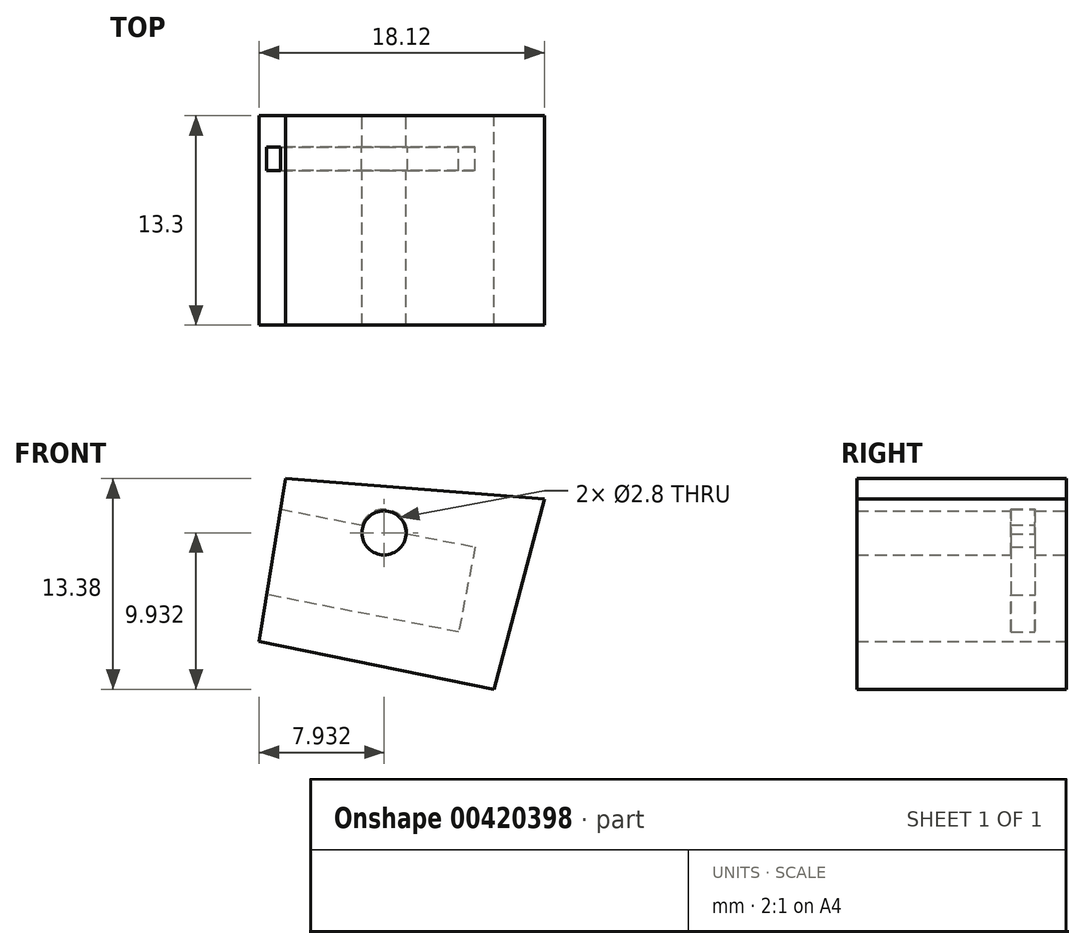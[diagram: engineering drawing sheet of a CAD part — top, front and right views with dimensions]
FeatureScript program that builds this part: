
annotation { "Feature Type Name" : "Feature", "Feature Type Description" : "" }
export const myFeature = defineFeature(function(context is Context, id is Id, definition is map)
    precondition{}
    {
        {
            var Q0;
            Q0=qCreatedBy(makeId("Front.planeOp"),FACE);
            var sketch = newSketch(context, id + "F0", { "sketchPlane" : qUnion([Q0])});
            skArc(sketch, "E0", {"start": v(0.13, 4.4) * mm, "mid": v(0, 4.4) * mm, "end": v(-0.13, 4.4) * mm});
            skLineSegment(sketch, "E1", {"start": v(0.28, 4.51) * mm, "end": v(0.42, 5.1) * mm});
            skLineSegment(sketch, "E2.MirrorCS", {"start": v(-0.28, 4.51) * mm, "end": v(-0.42, 5.1) * mm});
            skPoint(sketch, "E3.visualSharp", {"position": v(0.25, 4.4) * mm});
            skArc(sketch, "E3.filletArc", {"start": v(0.13, 4.4) * mm, "mid": v(0.22, 4.43) * mm, "end": v(0.28, 4.51) * mm});
            skPoint(sketch, "E4.visualSharp", {"position": v(-0.25, 4.4) * mm});
            skArc(sketch, "E4.filletArc", {"start": v(-0.28, 4.51) * mm, "mid": v(-0.22, 4.43) * mm, "end": v(-0.13, 4.4) * mm});
            skPoint(sketch, "E5.visualSharp", {"position": v(0.45, 5.23) * mm});
            skArc(sketch, "E5.filletArc", {"start": v(0.58, 5.22) * mm, "mid": v(0.48, 5.2) * mm, "end": v(0.42, 5.1) * mm});
            skPoint(sketch, "E6.visualSharp", {"position": v(-0.45, 5.23) * mm});
            skArc(sketch, "E6.filletArc", {"start": v(-0.42, 5.1) * mm, "mid": v(-0.48, 5.2) * mm, "end": v(-0.58, 5.22) * mm});
            skArc(sketch, "E7.trimOffspring", {"start": v(1.46, 5.04) * mm, "mid": v(1.02, 5.15) * mm, "end": v(0.58, 5.22) * mm});
            skPoint(sketch, "E8.visualSharp", {"position": v(1.59, 5) * mm});
            skArc(sketch, "E9.1.1", {"start": v(-1.98, 4.06) * mm, "mid": v(-1.9, 4) * mm, "end": v(-1.8, 4.01) * mm});
            skArc(sketch, "E9.1.2", {"start": v(-0.58, 5.22) * mm, "mid": v(-1.02, 5.15) * mm, "end": v(-1.46, 5.04) * mm});
            skArc(sketch, "E9.1.3", {"start": v(-1.56, 4.11) * mm, "mid": v(-1.68, 4.07) * mm, "end": v(-1.8, 4.01) * mm});
            skLineSegment(sketch, "E9.1.4", {"start": v(-1.98, 4.06) * mm, "end": v(-2.34, 4.55) * mm});
            skPoint(sketch, "E9.1.5", {"position": v(-1.91, 3.96) * mm});
            skPoint(sketch, "E9.1.6", {"position": v(-2.42, 4.66) * mm});
            skLineSegment(sketch, "E9.1.7", {"start": v(-1.47, 4.28) * mm, "end": v(-1.57, 4.88) * mm});
            skPoint(sketch, "E9.1.8", {"position": v(-1.59, 5) * mm});
            skArc(sketch, "E9.1.9", {"start": v(-1.56, 4.11) * mm, "mid": v(-1.49, 4.18) * mm, "end": v(-1.47, 4.28) * mm});
            skArc(sketch, "E9.1.10", {"start": v(-1.46, 5.04) * mm, "mid": v(-1.54, 4.98) * mm, "end": v(-1.57, 4.88) * mm});
            skPoint(sketch, "E9.1.11", {"position": v(-1.45, 4.15) * mm});
            skArc(sketch, "E9.1.12", {"start": v(-2.34, 4.55) * mm, "mid": v(-2.43, 4.61) * mm, "end": v(-2.53, 4.6) * mm});
            skPoint(sketch, "E9.2.0", {"position": v(-2.42, 4.66) * mm});
            skArc(sketch, "E9.2.1", {"start": v(-3.39, 3) * mm, "mid": v(-3.3, 2.97) * mm, "end": v(-3.2, 3.02) * mm});
            skArc(sketch, "E9.2.2", {"start": v(-2.53, 4.6) * mm, "mid": v(-2.92, 4.37) * mm, "end": v(-3.28, 4.1) * mm});
            skArc(sketch, "E9.2.3", {"start": v(-3.02, 3.2) * mm, "mid": v(-3.11, 3.11) * mm, "end": v(-3.2, 3.02) * mm});
            skLineSegment(sketch, "E9.2.4", {"start": v(-3.39, 3) * mm, "end": v(-3.9, 3.31) * mm});
            skPoint(sketch, "E9.2.5", {"position": v(-3.28, 2.93) * mm});
            skPoint(sketch, "E9.2.6", {"position": v(-4.02, 3.38) * mm});
            skLineSegment(sketch, "E9.2.7", {"start": v(-3, 3.39) * mm, "end": v(-3.31, 3.9) * mm});
            skPoint(sketch, "E9.2.8", {"position": v(-3.38, 4.02) * mm});
            skArc(sketch, "E9.2.9", {"start": v(-3.02, 3.2) * mm, "mid": v(-2.97, 3.3) * mm, "end": v(-3, 3.39) * mm});
            skArc(sketch, "E9.2.10", {"start": v(-3.28, 4.1) * mm, "mid": v(-3.33, 4) * mm, "end": v(-3.31, 3.9) * mm});
            skPoint(sketch, "E9.2.11", {"position": v(-2.93, 3.28) * mm});
            skArc(sketch, "E9.2.12", {"start": v(-3.9, 3.31) * mm, "mid": v(-4, 3.33) * mm, "end": v(-4.1, 3.28) * mm});
            skPoint(sketch, "E9.3.0", {"position": v(-4.02, 3.38) * mm});
            skArc(sketch, "E9.3.1", {"start": v(-4.28, 1.47) * mm, "mid": v(-4.18, 1.49) * mm, "end": v(-4.11, 1.56) * mm});
            skArc(sketch, "E9.3.2", {"start": v(-4.1, 3.28) * mm, "mid": v(-4.37, 2.92) * mm, "end": v(-4.6, 2.53) * mm});
            skArc(sketch, "E9.3.3", {"start": v(-4.01, 1.8) * mm, "mid": v(-4.07, 1.68) * mm, "end": v(-4.11, 1.56) * mm});
            skLineSegment(sketch, "E9.3.4", {"start": v(-4.28, 1.47) * mm, "end": v(-4.88, 1.57) * mm});
            skPoint(sketch, "E9.3.5", {"position": v(-4.15, 1.45) * mm});
            skPoint(sketch, "E9.3.6", {"position": v(-5, 1.59) * mm});
            skLineSegment(sketch, "E9.3.7", {"start": v(-4.06, 1.98) * mm, "end": v(-4.55, 2.34) * mm});
            skPoint(sketch, "E9.3.8", {"position": v(-4.66, 2.42) * mm});
            skArc(sketch, "E9.3.9", {"start": v(-4.01, 1.8) * mm, "mid": v(-4, 1.9) * mm, "end": v(-4.06, 1.98) * mm});
            skArc(sketch, "E9.3.10", {"start": v(-4.6, 2.53) * mm, "mid": v(-4.61, 2.43) * mm, "end": v(-4.55, 2.34) * mm});
            skPoint(sketch, "E9.3.11", {"position": v(-3.96, 1.91) * mm});
            skArc(sketch, "E9.3.12", {"start": v(-4.88, 1.57) * mm, "mid": v(-4.98, 1.54) * mm, "end": v(-5.04, 1.46) * mm});
            skPoint(sketch, "E9.4.0", {"position": v(-5, 1.59) * mm});
            skArc(sketch, "E9.4.1", {"start": v(-4.51, -0.28) * mm, "mid": v(-4.43, -0.22) * mm, "end": v(-4.4, -0.13) * mm});
            skArc(sketch, "E9.4.2", {"start": v(-5.04, 1.46) * mm, "mid": v(-5.15, 1.02) * mm, "end": v(-5.22, 0.58) * mm});
            skArc(sketch, "E9.4.3", {"start": v(-4.4, 0.13) * mm, "mid": v(-4.4, 0) * mm, "end": v(-4.4, -0.13) * mm});
            skLineSegment(sketch, "E9.4.4", {"start": v(-4.51, -0.28) * mm, "end": v(-5.1, -0.42) * mm});
            skPoint(sketch, "E9.4.5", {"position": v(-4.4, -0.25) * mm});
            skPoint(sketch, "E9.4.6", {"position": v(-5.23, -0.45) * mm});
            skLineSegment(sketch, "E9.4.7", {"start": v(-4.51, 0.28) * mm, "end": v(-5.1, 0.42) * mm});
            skPoint(sketch, "E9.4.8", {"position": v(-5.23, 0.45) * mm});
            skArc(sketch, "E9.4.9", {"start": v(-4.4, 0.13) * mm, "mid": v(-4.43, 0.22) * mm, "end": v(-4.51, 0.28) * mm});
            skArc(sketch, "E9.4.10", {"start": v(-5.22, 0.58) * mm, "mid": v(-5.2, 0.48) * mm, "end": v(-5.1, 0.42) * mm});
            skPoint(sketch, "E9.4.11", {"position": v(-4.4, 0.25) * mm});
            skArc(sketch, "E9.4.12", {"start": v(-5.1, -0.42) * mm, "mid": v(-5.2, -0.48) * mm, "end": v(-5.22, -0.58) * mm});
            skPoint(sketch, "E9.5.0", {"position": v(-5.23, -0.45) * mm});
            skArc(sketch, "E9.5.1", {"start": v(-4.06, -1.98) * mm, "mid": v(-4, -1.9) * mm, "end": v(-4.01, -1.8) * mm});
            skArc(sketch, "E9.5.2", {"start": v(-5.22, -0.58) * mm, "mid": v(-5.15, -1.02) * mm, "end": v(-5.04, -1.46) * mm});
            skArc(sketch, "E9.5.3", {"start": v(-4.11, -1.56) * mm, "mid": v(-4.07, -1.68) * mm, "end": v(-4.01, -1.8) * mm});
            skLineSegment(sketch, "E9.5.4", {"start": v(-4.06, -1.98) * mm, "end": v(-4.55, -2.34) * mm});
            skPoint(sketch, "E9.5.5", {"position": v(-3.96, -1.91) * mm});
            skPoint(sketch, "E9.5.6", {"position": v(-4.66, -2.42) * mm});
            skLineSegment(sketch, "E9.5.7", {"start": v(-4.28, -1.47) * mm, "end": v(-4.88, -1.57) * mm});
            skPoint(sketch, "E9.5.8", {"position": v(-5, -1.59) * mm});
            skArc(sketch, "E9.5.9", {"start": v(-4.11, -1.56) * mm, "mid": v(-4.18, -1.49) * mm, "end": v(-4.28, -1.47) * mm});
            skArc(sketch, "E9.5.10", {"start": v(-5.04, -1.46) * mm, "mid": v(-4.98, -1.54) * mm, "end": v(-4.88, -1.57) * mm});
            skPoint(sketch, "E9.5.11", {"position": v(-4.15, -1.45) * mm});
            skArc(sketch, "E9.5.12", {"start": v(-4.55, -2.34) * mm, "mid": v(-4.61, -2.43) * mm, "end": v(-4.6, -2.53) * mm});
            skPoint(sketch, "E9.6.0", {"position": v(-4.66, -2.42) * mm});
            skArc(sketch, "E9.6.1", {"start": v(-3, -3.39) * mm, "mid": v(-2.97, -3.3) * mm, "end": v(-3.02, -3.2) * mm});
            skArc(sketch, "E9.6.2", {"start": v(-4.6, -2.53) * mm, "mid": v(-4.37, -2.92) * mm, "end": v(-4.1, -3.28) * mm});
            skArc(sketch, "E9.6.3", {"start": v(-3.2, -3.02) * mm, "mid": v(-3.11, -3.11) * mm, "end": v(-3.02, -3.2) * mm});
            skLineSegment(sketch, "E9.6.4", {"start": v(-3, -3.39) * mm, "end": v(-3.31, -3.9) * mm});
            skPoint(sketch, "E9.6.5", {"position": v(-2.93, -3.28) * mm});
            skPoint(sketch, "E9.6.6", {"position": v(-3.38, -4.02) * mm});
            skLineSegment(sketch, "E9.6.7", {"start": v(-3.39, -3) * mm, "end": v(-3.9, -3.31) * mm});
            skPoint(sketch, "E9.6.8", {"position": v(-4.02, -3.38) * mm});
            skArc(sketch, "E9.6.9", {"start": v(-3.2, -3.02) * mm, "mid": v(-3.3, -2.97) * mm, "end": v(-3.39, -3) * mm});
            skArc(sketch, "E9.6.10", {"start": v(-4.1, -3.28) * mm, "mid": v(-4, -3.33) * mm, "end": v(-3.9, -3.31) * mm});
            skPoint(sketch, "E9.6.11", {"position": v(-3.28, -2.93) * mm});
            skArc(sketch, "E9.6.12", {"start": v(-3.31, -3.9) * mm, "mid": v(-3.33, -4) * mm, "end": v(-3.28, -4.1) * mm});
            skPoint(sketch, "E9.7.0", {"position": v(-3.38, -4.02) * mm});
            skArc(sketch, "E9.7.1", {"start": v(-1.47, -4.28) * mm, "mid": v(-1.49, -4.18) * mm, "end": v(-1.56, -4.11) * mm});
            skArc(sketch, "E9.7.2", {"start": v(-3.28, -4.1) * mm, "mid": v(-2.92, -4.37) * mm, "end": v(-2.53, -4.6) * mm});
            skArc(sketch, "E9.7.3", {"start": v(-1.8, -4.01) * mm, "mid": v(-1.68, -4.07) * mm, "end": v(-1.56, -4.11) * mm});
            skLineSegment(sketch, "E9.7.4", {"start": v(-1.47, -4.28) * mm, "end": v(-1.57, -4.88) * mm});
            skPoint(sketch, "E9.7.5", {"position": v(-1.45, -4.15) * mm});
            skPoint(sketch, "E9.7.6", {"position": v(-1.59, -5) * mm});
            skLineSegment(sketch, "E9.7.7", {"start": v(-1.98, -4.06) * mm, "end": v(-2.34, -4.55) * mm});
            skPoint(sketch, "E9.7.8", {"position": v(-2.42, -4.66) * mm});
            skArc(sketch, "E9.7.9", {"start": v(-1.8, -4.01) * mm, "mid": v(-1.9, -4) * mm, "end": v(-1.98, -4.06) * mm});
            skArc(sketch, "E9.7.10", {"start": v(-2.53, -4.6) * mm, "mid": v(-2.43, -4.61) * mm, "end": v(-2.34, -4.55) * mm});
            skPoint(sketch, "E9.7.11", {"position": v(-1.91, -3.96) * mm});
            skArc(sketch, "E9.7.12", {"start": v(-1.57, -4.88) * mm, "mid": v(-1.54, -4.98) * mm, "end": v(-1.46, -5.04) * mm});
            skPoint(sketch, "E9.8.0", {"position": v(-1.59, -5) * mm});
            skArc(sketch, "E9.8.1", {"start": v(0.28, -4.51) * mm, "mid": v(0.22, -4.43) * mm, "end": v(0.13, -4.4) * mm});
            skArc(sketch, "E9.8.2", {"start": v(-1.46, -5.04) * mm, "mid": v(-1.02, -5.15) * mm, "end": v(-0.58, -5.22) * mm});
            skArc(sketch, "E9.8.3", {"start": v(-0.13, -4.4) * mm, "mid": v(0, -4.4) * mm, "end": v(0.13, -4.4) * mm});
            skLineSegment(sketch, "E9.8.4", {"start": v(0.28, -4.51) * mm, "end": v(0.42, -5.1) * mm});
            skPoint(sketch, "E9.8.5", {"position": v(0.25, -4.4) * mm});
            skPoint(sketch, "E9.8.6", {"position": v(0.45, -5.23) * mm});
            skLineSegment(sketch, "E9.8.7", {"start": v(-0.28, -4.51) * mm, "end": v(-0.42, -5.1) * mm});
            skPoint(sketch, "E9.8.8", {"position": v(-0.45, -5.23) * mm});
            skArc(sketch, "E9.8.9", {"start": v(-0.13, -4.4) * mm, "mid": v(-0.22, -4.43) * mm, "end": v(-0.28, -4.51) * mm});
            skArc(sketch, "E9.8.10", {"start": v(-0.58, -5.22) * mm, "mid": v(-0.48, -5.2) * mm, "end": v(-0.42, -5.1) * mm});
            skPoint(sketch, "E9.8.11", {"position": v(-0.25, -4.4) * mm});
            skArc(sketch, "E9.8.12", {"start": v(0.42, -5.1) * mm, "mid": v(0.48, -5.2) * mm, "end": v(0.58, -5.22) * mm});
            skPoint(sketch, "E9.9.0", {"position": v(0.45, -5.23) * mm});
            skArc(sketch, "E9.9.1", {"start": v(1.98, -4.06) * mm, "mid": v(1.9, -4) * mm, "end": v(1.8, -4.01) * mm});
            skArc(sketch, "E9.9.2", {"start": v(0.58, -5.22) * mm, "mid": v(1.02, -5.15) * mm, "end": v(1.46, -5.04) * mm});
            skArc(sketch, "E9.9.3", {"start": v(1.56, -4.11) * mm, "mid": v(1.68, -4.07) * mm, "end": v(1.8, -4.01) * mm});
            skLineSegment(sketch, "E9.9.4", {"start": v(1.98, -4.06) * mm, "end": v(2.34, -4.55) * mm});
            skPoint(sketch, "E9.9.5", {"position": v(1.91, -3.96) * mm});
            skPoint(sketch, "E9.9.6", {"position": v(2.42, -4.66) * mm});
            skLineSegment(sketch, "E9.9.7", {"start": v(1.47, -4.28) * mm, "end": v(1.57, -4.88) * mm});
            skPoint(sketch, "E9.9.8", {"position": v(1.59, -5) * mm});
            skArc(sketch, "E9.9.9", {"start": v(1.56, -4.11) * mm, "mid": v(1.49, -4.18) * mm, "end": v(1.47, -4.28) * mm});
            skArc(sketch, "E9.9.10", {"start": v(1.46, -5.04) * mm, "mid": v(1.54, -4.98) * mm, "end": v(1.57, -4.88) * mm});
            skPoint(sketch, "E9.9.11", {"position": v(1.45, -4.15) * mm});
            skArc(sketch, "E9.9.12", {"start": v(2.34, -4.55) * mm, "mid": v(2.43, -4.61) * mm, "end": v(2.53, -4.6) * mm});
            skPoint(sketch, "E9.10.0", {"position": v(2.42, -4.66) * mm});
            skArc(sketch, "E9.10.1", {"start": v(3.39, -3) * mm, "mid": v(3.3, -2.97) * mm, "end": v(3.2, -3.02) * mm});
            skArc(sketch, "E9.10.2", {"start": v(2.53, -4.6) * mm, "mid": v(2.92, -4.37) * mm, "end": v(3.28, -4.1) * mm});
            skArc(sketch, "E9.10.3", {"start": v(3.02, -3.2) * mm, "mid": v(3.11, -3.11) * mm, "end": v(3.2, -3.02) * mm});
            skLineSegment(sketch, "E9.10.4", {"start": v(3.39, -3) * mm, "end": v(3.9, -3.31) * mm});
            skPoint(sketch, "E9.10.5", {"position": v(3.28, -2.93) * mm});
            skPoint(sketch, "E9.10.6", {"position": v(4.02, -3.38) * mm});
            skLineSegment(sketch, "E9.10.7", {"start": v(3, -3.39) * mm, "end": v(3.31, -3.9) * mm});
            skPoint(sketch, "E9.10.8", {"position": v(3.38, -4.02) * mm});
            skArc(sketch, "E9.10.9", {"start": v(3.02, -3.2) * mm, "mid": v(2.97, -3.3) * mm, "end": v(3, -3.39) * mm});
            skArc(sketch, "E9.10.10", {"start": v(3.28, -4.1) * mm, "mid": v(3.33, -4) * mm, "end": v(3.31, -3.9) * mm});
            skPoint(sketch, "E9.10.11", {"position": v(2.93, -3.28) * mm});
            skArc(sketch, "E9.10.12", {"start": v(3.9, -3.31) * mm, "mid": v(4, -3.33) * mm, "end": v(4.1, -3.28) * mm});
            skPoint(sketch, "E9.11.0", {"position": v(4.02, -3.38) * mm});
            skArc(sketch, "E9.11.1", {"start": v(4.28, -1.47) * mm, "mid": v(4.18, -1.49) * mm, "end": v(4.11, -1.56) * mm});
            skArc(sketch, "E9.11.2", {"start": v(4.1, -3.28) * mm, "mid": v(4.37, -2.92) * mm, "end": v(4.6, -2.53) * mm});
            skArc(sketch, "E9.11.3", {"start": v(4.01, -1.8) * mm, "mid": v(4.07, -1.68) * mm, "end": v(4.11, -1.56) * mm});
            skLineSegment(sketch, "E9.11.4", {"start": v(4.28, -1.47) * mm, "end": v(4.88, -1.57) * mm});
            skPoint(sketch, "E9.11.5", {"position": v(4.15, -1.45) * mm});
            skPoint(sketch, "E9.11.6", {"position": v(5, -1.59) * mm});
            skLineSegment(sketch, "E9.11.7", {"start": v(4.06, -1.98) * mm, "end": v(4.55, -2.34) * mm});
            skPoint(sketch, "E9.11.8", {"position": v(4.66, -2.42) * mm});
            skArc(sketch, "E9.11.9", {"start": v(4.01, -1.8) * mm, "mid": v(4, -1.9) * mm, "end": v(4.06, -1.98) * mm});
            skArc(sketch, "E9.11.10", {"start": v(4.6, -2.53) * mm, "mid": v(4.61, -2.43) * mm, "end": v(4.55, -2.34) * mm});
            skPoint(sketch, "E9.11.11", {"position": v(3.96, -1.91) * mm});
            skArc(sketch, "E9.11.12", {"start": v(4.88, -1.57) * mm, "mid": v(4.98, -1.54) * mm, "end": v(5.04, -1.46) * mm});
            skPoint(sketch, "E9.12.0", {"position": v(5, -1.59) * mm});
            skArc(sketch, "E9.12.1", {"start": v(4.51, 0.28) * mm, "mid": v(4.43, 0.22) * mm, "end": v(4.4, 0.13) * mm});
            skArc(sketch, "E9.12.2", {"start": v(5.04, -1.46) * mm, "mid": v(5.15, -1.02) * mm, "end": v(5.22, -0.58) * mm});
            skArc(sketch, "E9.12.3", {"start": v(4.4, -0.13) * mm, "mid": v(4.4, 0) * mm, "end": v(4.4, 0.13) * mm});
            skLineSegment(sketch, "E9.12.4", {"start": v(4.51, 0.28) * mm, "end": v(5.1, 0.42) * mm});
            skPoint(sketch, "E9.12.5", {"position": v(4.4, 0.25) * mm});
            skPoint(sketch, "E9.12.6", {"position": v(5.23, 0.45) * mm});
            skLineSegment(sketch, "E9.12.7", {"start": v(4.51, -0.28) * mm, "end": v(5.1, -0.42) * mm});
            skPoint(sketch, "E9.12.8", {"position": v(5.23, -0.45) * mm});
            skArc(sketch, "E9.12.9", {"start": v(4.4, -0.13) * mm, "mid": v(4.43, -0.22) * mm, "end": v(4.51, -0.28) * mm});
            skArc(sketch, "E9.12.10", {"start": v(5.22, -0.58) * mm, "mid": v(5.2, -0.48) * mm, "end": v(5.1, -0.42) * mm});
            skPoint(sketch, "E9.12.11", {"position": v(4.4, -0.25) * mm});
            skArc(sketch, "E9.12.12", {"start": v(5.1, 0.42) * mm, "mid": v(5.2, 0.48) * mm, "end": v(5.22, 0.58) * mm});
            skPoint(sketch, "E9.13.0", {"position": v(5.23, 0.45) * mm});
            skArc(sketch, "E9.13.1", {"start": v(4.06, 1.98) * mm, "mid": v(4, 1.9) * mm, "end": v(4.01, 1.8) * mm});
            skArc(sketch, "E9.13.2", {"start": v(5.22, 0.58) * mm, "mid": v(5.15, 1.02) * mm, "end": v(5.04, 1.46) * mm});
            skArc(sketch, "E9.13.3", {"start": v(4.11, 1.56) * mm, "mid": v(4.07, 1.68) * mm, "end": v(4.01, 1.8) * mm});
            skLineSegment(sketch, "E9.13.4", {"start": v(4.06, 1.98) * mm, "end": v(4.55, 2.34) * mm});
            skPoint(sketch, "E9.13.5", {"position": v(3.96, 1.91) * mm});
            skPoint(sketch, "E9.13.6", {"position": v(4.66, 2.42) * mm});
            skLineSegment(sketch, "E9.13.7", {"start": v(4.28, 1.47) * mm, "end": v(4.88, 1.57) * mm});
            skPoint(sketch, "E9.13.8", {"position": v(5, 1.59) * mm});
            skArc(sketch, "E9.13.9", {"start": v(4.11, 1.56) * mm, "mid": v(4.18, 1.49) * mm, "end": v(4.28, 1.47) * mm});
            skArc(sketch, "E9.13.10", {"start": v(5.04, 1.46) * mm, "mid": v(4.98, 1.54) * mm, "end": v(4.88, 1.57) * mm});
            skPoint(sketch, "E9.13.11", {"position": v(4.15, 1.45) * mm});
            skArc(sketch, "E9.13.12", {"start": v(4.55, 2.34) * mm, "mid": v(4.61, 2.43) * mm, "end": v(4.6, 2.53) * mm});
            skPoint(sketch, "E9.14.0", {"position": v(4.66, 2.42) * mm});
            skArc(sketch, "E9.14.1", {"start": v(3, 3.39) * mm, "mid": v(2.97, 3.3) * mm, "end": v(3.02, 3.2) * mm});
            skArc(sketch, "E9.14.2", {"start": v(4.6, 2.53) * mm, "mid": v(4.37, 2.92) * mm, "end": v(4.1, 3.28) * mm});
            skArc(sketch, "E9.14.3", {"start": v(3.2, 3.02) * mm, "mid": v(3.11, 3.11) * mm, "end": v(3.02, 3.2) * mm});
            skLineSegment(sketch, "E9.14.4", {"start": v(3, 3.39) * mm, "end": v(3.31, 3.9) * mm});
            skPoint(sketch, "E9.14.5", {"position": v(2.93, 3.28) * mm});
            skPoint(sketch, "E9.14.6", {"position": v(3.38, 4.02) * mm});
            skLineSegment(sketch, "E9.14.7", {"start": v(3.39, 3) * mm, "end": v(3.9, 3.31) * mm});
            skPoint(sketch, "E9.14.8", {"position": v(4.02, 3.38) * mm});
            skArc(sketch, "E9.14.9", {"start": v(3.2, 3.02) * mm, "mid": v(3.3, 2.97) * mm, "end": v(3.39, 3) * mm});
            skArc(sketch, "E9.14.10", {"start": v(4.1, 3.28) * mm, "mid": v(4, 3.33) * mm, "end": v(3.9, 3.31) * mm});
            skPoint(sketch, "E9.14.11", {"position": v(3.28, 2.93) * mm});
            skArc(sketch, "E9.14.12", {"start": v(3.31, 3.9) * mm, "mid": v(3.33, 4) * mm, "end": v(3.28, 4.1) * mm});
            skPoint(sketch, "E9.15.0", {"position": v(3.38, 4.02) * mm});
            skArc(sketch, "E9.15.1", {"start": v(1.47, 4.28) * mm, "mid": v(1.49, 4.18) * mm, "end": v(1.56, 4.11) * mm});
            skArc(sketch, "E9.15.2", {"start": v(3.28, 4.1) * mm, "mid": v(2.92, 4.37) * mm, "end": v(2.53, 4.6) * mm});
            skArc(sketch, "E9.15.3", {"start": v(1.8, 4.01) * mm, "mid": v(1.68, 4.07) * mm, "end": v(1.56, 4.11) * mm});
            skLineSegment(sketch, "E9.15.4", {"start": v(1.47, 4.28) * mm, "end": v(1.57, 4.88) * mm});
            skPoint(sketch, "E9.15.5", {"position": v(1.45, 4.15) * mm});
            skLineSegment(sketch, "E9.15.7", {"start": v(1.98, 4.06) * mm, "end": v(2.34, 4.55) * mm});
            skPoint(sketch, "E9.15.8", {"position": v(2.42, 4.66) * mm});
            skArc(sketch, "E9.15.9", {"start": v(1.8, 4.01) * mm, "mid": v(1.9, 4) * mm, "end": v(1.98, 4.06) * mm});
            skArc(sketch, "E9.15.10", {"start": v(2.53, 4.6) * mm, "mid": v(2.43, 4.61) * mm, "end": v(2.34, 4.55) * mm});
            skPoint(sketch, "E9.15.11", {"position": v(1.91, 3.96) * mm});
            skArc(sketch, "E9.15.12", {"start": v(1.57, 4.88) * mm, "mid": v(1.54, 4.98) * mm, "end": v(1.46, 5.04) * mm});
            skCircle(sketch, "E10", {"center": v(0, 0) * mm, "radius": 7.5 * mm});
            skSolve(sketch);
        }
        {
            var Q0;
            Q0=qSketchRegion(id+"F0",true);
            extrude(context, id + "F1", {"entities" : qUnion([Q0]), "depth" : 10 * mm});
        }
        {
            var Q0;
            Q0=makeQuery(id+"F1.opExtrude","CAP_FACE",FACE,{"disambiguationData":[OSD([sQuery(id+"F0.wireOp",EDGE,"E0"),sQuery(id+"F0.wireOp",EDGE,"E1"),sQuery(id+"F0.wireOp",EDGE,"E2.MirrorCS"),sQuery(id+"F0.wireOp",EDGE,"E3.filletArc"),sQuery(id+"F0.wireOp",EDGE,"E4.filletArc"),sQuery(id+"F0.wireOp",EDGE,"E5.filletArc"),sQuery(id+"F0.wireOp",EDGE,"E6.filletArc"),sQuery(id+"F0.wireOp",EDGE,"E7.trimOffspring"),sQuery(id+"F0.wireOp",EDGE,"E9.1.1"),sQuery(id+"F0.wireOp",EDGE,"E9.1.2"),sQuery(id+"F0.wireOp",EDGE,"E9.1.3"),sQuery(id+"F0.wireOp",EDGE,"E9.1.4"),sQuery(id+"F0.wireOp",EDGE,"E9.1.7"),sQuery(id+"F0.wireOp",EDGE,"E9.1.9"),sQuery(id+"F0.wireOp",EDGE,"E9.1.10"),sQuery(id+"F0.wireOp",EDGE,"E9.1.12"),sQuery(id+"F0.wireOp",EDGE,"E9.2.1"),sQuery(id+"F0.wireOp",EDGE,"E9.2.2"),sQuery(id+"F0.wireOp",EDGE,"E9.2.3"),sQuery(id+"F0.wireOp",EDGE,"E9.2.4"),sQuery(id+"F0.wireOp",EDGE,"E9.2.7"),sQuery(id+"F0.wireOp",EDGE,"E9.2.9"),sQuery(id+"F0.wireOp",EDGE,"E9.2.10"),sQuery(id+"F0.wireOp",EDGE,"E9.2.12"),sQuery(id+"F0.wireOp",EDGE,"E9.3.1"),sQuery(id+"F0.wireOp",EDGE,"E9.3.2"),sQuery(id+"F0.wireOp",EDGE,"E9.3.3"),sQuery(id+"F0.wireOp",EDGE,"E9.3.4"),sQuery(id+"F0.wireOp",EDGE,"E9.3.7"),sQuery(id+"F0.wireOp",EDGE,"E9.3.9"),sQuery(id+"F0.wireOp",EDGE,"E9.3.10"),sQuery(id+"F0.wireOp",EDGE,"E9.3.12"),sQuery(id+"F0.wireOp",EDGE,"E9.4.1"),sQuery(id+"F0.wireOp",EDGE,"E9.4.2"),sQuery(id+"F0.wireOp",EDGE,"E9.4.3"),sQuery(id+"F0.wireOp",EDGE,"E9.4.4"),sQuery(id+"F0.wireOp",EDGE,"E9.4.7"),sQuery(id+"F0.wireOp",EDGE,"E9.4.9"),sQuery(id+"F0.wireOp",EDGE,"E9.4.10"),sQuery(id+"F0.wireOp",EDGE,"E9.4.12"),sQuery(id+"F0.wireOp",EDGE,"E9.5.1"),sQuery(id+"F0.wireOp",EDGE,"E9.5.2"),sQuery(id+"F0.wireOp",EDGE,"E9.5.3"),sQuery(id+"F0.wireOp",EDGE,"E9.5.4"),sQuery(id+"F0.wireOp",EDGE,"E9.5.7"),sQuery(id+"F0.wireOp",EDGE,"E9.5.9"),sQuery(id+"F0.wireOp",EDGE,"E9.5.10"),sQuery(id+"F0.wireOp",EDGE,"E9.5.12"),sQuery(id+"F0.wireOp",EDGE,"E9.6.1"),sQuery(id+"F0.wireOp",EDGE,"E9.6.2"),sQuery(id+"F0.wireOp",EDGE,"E9.6.3"),sQuery(id+"F0.wireOp",EDGE,"E9.6.4"),sQuery(id+"F0.wireOp",EDGE,"E9.6.7"),sQuery(id+"F0.wireOp",EDGE,"E9.6.9"),sQuery(id+"F0.wireOp",EDGE,"E9.6.10"),sQuery(id+"F0.wireOp",EDGE,"E9.6.12"),sQuery(id+"F0.wireOp",EDGE,"E9.7.1"),sQuery(id+"F0.wireOp",EDGE,"E9.7.2"),sQuery(id+"F0.wireOp",EDGE,"E9.7.3"),sQuery(id+"F0.wireOp",EDGE,"E9.7.4"),sQuery(id+"F0.wireOp",EDGE,"E9.7.7"),sQuery(id+"F0.wireOp",EDGE,"E9.7.9"),sQuery(id+"F0.wireOp",EDGE,"E9.7.10"),sQuery(id+"F0.wireOp",EDGE,"E9.7.12"),sQuery(id+"F0.wireOp",EDGE,"E9.8.1"),sQuery(id+"F0.wireOp",EDGE,"E9.8.2"),sQuery(id+"F0.wireOp",EDGE,"E9.8.3"),sQuery(id+"F0.wireOp",EDGE,"E9.8.4"),sQuery(id+"F0.wireOp",EDGE,"E9.8.7"),sQuery(id+"F0.wireOp",EDGE,"E9.8.9"),sQuery(id+"F0.wireOp",EDGE,"E9.8.10"),sQuery(id+"F0.wireOp",EDGE,"E9.8.12"),sQuery(id+"F0.wireOp",EDGE,"E9.9.1"),sQuery(id+"F0.wireOp",EDGE,"E9.9.2"),sQuery(id+"F0.wireOp",EDGE,"E9.9.3"),sQuery(id+"F0.wireOp",EDGE,"E9.9.4"),sQuery(id+"F0.wireOp",EDGE,"E9.9.7"),sQuery(id+"F0.wireOp",EDGE,"E9.9.9"),sQuery(id+"F0.wireOp",EDGE,"E9.9.10"),sQuery(id+"F0.wireOp",EDGE,"E9.9.12"),sQuery(id+"F0.wireOp",EDGE,"E9.10.1"),sQuery(id+"F0.wireOp",EDGE,"E9.10.2"),sQuery(id+"F0.wireOp",EDGE,"E9.10.3"),sQuery(id+"F0.wireOp",EDGE,"E9.10.4"),sQuery(id+"F0.wireOp",EDGE,"E9.10.7"),sQuery(id+"F0.wireOp",EDGE,"E9.10.9"),sQuery(id+"F0.wireOp",EDGE,"E9.10.10"),sQuery(id+"F0.wireOp",EDGE,"E9.10.12"),sQuery(id+"F0.wireOp",EDGE,"E9.11.1"),sQuery(id+"F0.wireOp",EDGE,"E9.11.2"),sQuery(id+"F0.wireOp",EDGE,"E9.11.3"),sQuery(id+"F0.wireOp",EDGE,"E9.11.4"),sQuery(id+"F0.wireOp",EDGE,"E9.11.7"),sQuery(id+"F0.wireOp",EDGE,"E9.11.9"),sQuery(id+"F0.wireOp",EDGE,"E9.11.10"),sQuery(id+"F0.wireOp",EDGE,"E9.11.12"),sQuery(id+"F0.wireOp",EDGE,"E9.12.1"),sQuery(id+"F0.wireOp",EDGE,"E9.12.2"),sQuery(id+"F0.wireOp",EDGE,"E9.12.3"),sQuery(id+"F0.wireOp",EDGE,"E9.12.4"),sQuery(id+"F0.wireOp",EDGE,"E9.12.7"),sQuery(id+"F0.wireOp",EDGE,"E9.12.9"),sQuery(id+"F0.wireOp",EDGE,"E9.12.10"),sQuery(id+"F0.wireOp",EDGE,"E9.12.12"),sQuery(id+"F0.wireOp",EDGE,"E9.13.1"),sQuery(id+"F0.wireOp",EDGE,"E9.13.2"),sQuery(id+"F0.wireOp",EDGE,"E9.13.3"),sQuery(id+"F0.wireOp",EDGE,"E9.13.4"),sQuery(id+"F0.wireOp",EDGE,"E9.13.7"),sQuery(id+"F0.wireOp",EDGE,"E9.13.9"),sQuery(id+"F0.wireOp",EDGE,"E9.13.10"),sQuery(id+"F0.wireOp",EDGE,"E9.13.12"),sQuery(id+"F0.wireOp",EDGE,"E9.14.1"),sQuery(id+"F0.wireOp",EDGE,"E9.14.2"),sQuery(id+"F0.wireOp",EDGE,"E9.14.3"),sQuery(id+"F0.wireOp",EDGE,"E9.14.4"),sQuery(id+"F0.wireOp",EDGE,"E9.14.7"),sQuery(id+"F0.wireOp",EDGE,"E9.14.9"),sQuery(id+"F0.wireOp",EDGE,"E9.14.10"),sQuery(id+"F0.wireOp",EDGE,"E9.14.12"),sQuery(id+"F0.wireOp",EDGE,"E9.15.1"),sQuery(id+"F0.wireOp",EDGE,"E9.15.2"),sQuery(id+"F0.wireOp",EDGE,"E9.15.3"),sQuery(id+"F0.wireOp",EDGE,"E9.15.4"),sQuery(id+"F0.wireOp",EDGE,"E9.15.7"),sQuery(id+"F0.wireOp",EDGE,"E9.15.9"),sQuery(id+"F0.wireOp",EDGE,"E9.15.10"),sQuery(id+"F0.wireOp",EDGE,"E9.15.12"),sQuery(id+"F0.wireOp",EDGE,"E10")])],"isStart":false});
            var sketch = newSketch(context, id + "F2", { "sketchPlane" : qUnion([Q0])});
            skArc(sketch, "E11", {"start": v(72.38, -28.85) * mm, "mid": v(71.17, -27.32) * mm, "end": v(69.47, -28.29) * mm});
            skPoint(sketch, "E12.orphan", {"position": v(59.69, -35.02) * mm});
            skPoint(sketch, "E13.orphan", {"position": v(63.63, -25.26) * mm});
            skLineSegment(sketch, "E14", {"start": v(64.62, -25.34) * mm, "end": v(81.07, -26.63) * mm});
            skLineSegment(sketch, "E15", {"start": v(62.95, -35.68) * mm, "end": v(77.88, -38.72) * mm});
            skLineSegment(sketch, "E16", {"start": v(64.62, -25.34) * mm, "end": v(64.3, -27.28) * mm});
            skLineSegment(sketch, "E17", {"start": v(64.3, -27.28) * mm, "end": v(69.47, -28.29) * mm});
            skLineSegment(sketch, "E18", {"start": v(76.67, -29.68) * mm, "end": v(75.62, -35.08) * mm});
            skLineSegment(sketch, "E19", {"start": v(75.62, -35.08) * mm, "end": v(63.43, -32.72) * mm});
            skLineSegment(sketch, "E20.trimOffspring", {"start": v(63.43, -32.72) * mm, "end": v(62.95, -35.68) * mm});
            skLineSegment(sketch, "E21.trimOffspring", {"start": v(72.38, -28.85) * mm, "end": v(76.67, -29.68) * mm});
            skLineSegment(sketch, "E22", {"start": v(81.07, -26.63) * mm, "end": v(77.88, -38.72) * mm});
            skPoint(sketch, "E23.center.orphan", {"position": v(46.18, -23.89) * mm});
            skSolve(sketch);
        }
        {
            var Q0;
            Q0=makeQuery(id+"F1.opExtrude","SWEPT_BODY",BODY,{"disambiguationData":[OSD([sQuery(id+"F0.wireOp",EDGE,"E0"),sQuery(id+"F0.wireOp",EDGE,"E1"),sQuery(id+"F0.wireOp",EDGE,"E2.MirrorCS"),sQuery(id+"F0.wireOp",EDGE,"E3.filletArc"),sQuery(id+"F0.wireOp",EDGE,"E4.filletArc"),sQuery(id+"F0.wireOp",EDGE,"E5.filletArc"),sQuery(id+"F0.wireOp",EDGE,"E6.filletArc"),sQuery(id+"F0.wireOp",EDGE,"E7.trimOffspring"),sQuery(id+"F0.wireOp",EDGE,"E9.1.1"),sQuery(id+"F0.wireOp",EDGE,"E9.1.2"),sQuery(id+"F0.wireOp",EDGE,"E9.1.3"),sQuery(id+"F0.wireOp",EDGE,"E9.1.4"),sQuery(id+"F0.wireOp",EDGE,"E9.1.7"),sQuery(id+"F0.wireOp",EDGE,"E9.1.9"),sQuery(id+"F0.wireOp",EDGE,"E9.1.10"),sQuery(id+"F0.wireOp",EDGE,"E9.1.12"),sQuery(id+"F0.wireOp",EDGE,"E9.2.1"),sQuery(id+"F0.wireOp",EDGE,"E9.2.2"),sQuery(id+"F0.wireOp",EDGE,"E9.2.3"),sQuery(id+"F0.wireOp",EDGE,"E9.2.4"),sQuery(id+"F0.wireOp",EDGE,"E9.2.7"),sQuery(id+"F0.wireOp",EDGE,"E9.2.9"),sQuery(id+"F0.wireOp",EDGE,"E9.2.10"),sQuery(id+"F0.wireOp",EDGE,"E9.2.12"),sQuery(id+"F0.wireOp",EDGE,"E9.3.1"),sQuery(id+"F0.wireOp",EDGE,"E9.3.2"),sQuery(id+"F0.wireOp",EDGE,"E9.3.3"),sQuery(id+"F0.wireOp",EDGE,"E9.3.4"),sQuery(id+"F0.wireOp",EDGE,"E9.3.7"),sQuery(id+"F0.wireOp",EDGE,"E9.3.9"),sQuery(id+"F0.wireOp",EDGE,"E9.3.10"),sQuery(id+"F0.wireOp",EDGE,"E9.3.12"),sQuery(id+"F0.wireOp",EDGE,"E9.4.1"),sQuery(id+"F0.wireOp",EDGE,"E9.4.2"),sQuery(id+"F0.wireOp",EDGE,"E9.4.3"),sQuery(id+"F0.wireOp",EDGE,"E9.4.4"),sQuery(id+"F0.wireOp",EDGE,"E9.4.7"),sQuery(id+"F0.wireOp",EDGE,"E9.4.9"),sQuery(id+"F0.wireOp",EDGE,"E9.4.10"),sQuery(id+"F0.wireOp",EDGE,"E9.4.12"),sQuery(id+"F0.wireOp",EDGE,"E9.5.1"),sQuery(id+"F0.wireOp",EDGE,"E9.5.2"),sQuery(id+"F0.wireOp",EDGE,"E9.5.3"),sQuery(id+"F0.wireOp",EDGE,"E9.5.4"),sQuery(id+"F0.wireOp",EDGE,"E9.5.7"),sQuery(id+"F0.wireOp",EDGE,"E9.5.9"),sQuery(id+"F0.wireOp",EDGE,"E9.5.10"),sQuery(id+"F0.wireOp",EDGE,"E9.5.12"),sQuery(id+"F0.wireOp",EDGE,"E9.6.1"),sQuery(id+"F0.wireOp",EDGE,"E9.6.2"),sQuery(id+"F0.wireOp",EDGE,"E9.6.3"),sQuery(id+"F0.wireOp",EDGE,"E9.6.4"),sQuery(id+"F0.wireOp",EDGE,"E9.6.7"),sQuery(id+"F0.wireOp",EDGE,"E9.6.9"),sQuery(id+"F0.wireOp",EDGE,"E9.6.10"),sQuery(id+"F0.wireOp",EDGE,"E9.6.12"),sQuery(id+"F0.wireOp",EDGE,"E9.7.1"),sQuery(id+"F0.wireOp",EDGE,"E9.7.2"),sQuery(id+"F0.wireOp",EDGE,"E9.7.3"),sQuery(id+"F0.wireOp",EDGE,"E9.7.4"),sQuery(id+"F0.wireOp",EDGE,"E9.7.7"),sQuery(id+"F0.wireOp",EDGE,"E9.7.9"),sQuery(id+"F0.wireOp",EDGE,"E9.7.10"),sQuery(id+"F0.wireOp",EDGE,"E9.7.12"),sQuery(id+"F0.wireOp",EDGE,"E9.8.1"),sQuery(id+"F0.wireOp",EDGE,"E9.8.2"),sQuery(id+"F0.wireOp",EDGE,"E9.8.3"),sQuery(id+"F0.wireOp",EDGE,"E9.8.4"),sQuery(id+"F0.wireOp",EDGE,"E9.8.7"),sQuery(id+"F0.wireOp",EDGE,"E9.8.9"),sQuery(id+"F0.wireOp",EDGE,"E9.8.10"),sQuery(id+"F0.wireOp",EDGE,"E9.8.12"),sQuery(id+"F0.wireOp",EDGE,"E9.9.1"),sQuery(id+"F0.wireOp",EDGE,"E9.9.2"),sQuery(id+"F0.wireOp",EDGE,"E9.9.3"),sQuery(id+"F0.wireOp",EDGE,"E9.9.4"),sQuery(id+"F0.wireOp",EDGE,"E9.9.7"),sQuery(id+"F0.wireOp",EDGE,"E9.9.9"),sQuery(id+"F0.wireOp",EDGE,"E9.9.10"),sQuery(id+"F0.wireOp",EDGE,"E9.9.12"),sQuery(id+"F0.wireOp",EDGE,"E9.10.1"),sQuery(id+"F0.wireOp",EDGE,"E9.10.2"),sQuery(id+"F0.wireOp",EDGE,"E9.10.3"),sQuery(id+"F0.wireOp",EDGE,"E9.10.4"),sQuery(id+"F0.wireOp",EDGE,"E9.10.7"),sQuery(id+"F0.wireOp",EDGE,"E9.10.9"),sQuery(id+"F0.wireOp",EDGE,"E9.10.10"),sQuery(id+"F0.wireOp",EDGE,"E9.10.12"),sQuery(id+"F0.wireOp",EDGE,"E9.11.1"),sQuery(id+"F0.wireOp",EDGE,"E9.11.2"),sQuery(id+"F0.wireOp",EDGE,"E9.11.3"),sQuery(id+"F0.wireOp",EDGE,"E9.11.4"),sQuery(id+"F0.wireOp",EDGE,"E9.11.7"),sQuery(id+"F0.wireOp",EDGE,"E9.11.9"),sQuery(id+"F0.wireOp",EDGE,"E9.11.10"),sQuery(id+"F0.wireOp",EDGE,"E9.11.12"),sQuery(id+"F0.wireOp",EDGE,"E9.12.1"),sQuery(id+"F0.wireOp",EDGE,"E9.12.2"),sQuery(id+"F0.wireOp",EDGE,"E9.12.3"),sQuery(id+"F0.wireOp",EDGE,"E9.12.4"),sQuery(id+"F0.wireOp",EDGE,"E9.12.7"),sQuery(id+"F0.wireOp",EDGE,"E9.12.9"),sQuery(id+"F0.wireOp",EDGE,"E9.12.10"),sQuery(id+"F0.wireOp",EDGE,"E9.12.12"),sQuery(id+"F0.wireOp",EDGE,"E9.13.1"),sQuery(id+"F0.wireOp",EDGE,"E9.13.2"),sQuery(id+"F0.wireOp",EDGE,"E9.13.3"),sQuery(id+"F0.wireOp",EDGE,"E9.13.4"),sQuery(id+"F0.wireOp",EDGE,"E9.13.7"),sQuery(id+"F0.wireOp",EDGE,"E9.13.9"),sQuery(id+"F0.wireOp",EDGE,"E9.13.10"),sQuery(id+"F0.wireOp",EDGE,"E9.13.12"),sQuery(id+"F0.wireOp",EDGE,"E9.14.1"),sQuery(id+"F0.wireOp",EDGE,"E9.14.2"),sQuery(id+"F0.wireOp",EDGE,"E9.14.3"),sQuery(id+"F0.wireOp",EDGE,"E9.14.4"),sQuery(id+"F0.wireOp",EDGE,"E9.14.7"),sQuery(id+"F0.wireOp",EDGE,"E9.14.9"),sQuery(id+"F0.wireOp",EDGE,"E9.14.10"),sQuery(id+"F0.wireOp",EDGE,"E9.14.12"),sQuery(id+"F0.wireOp",EDGE,"E9.15.1"),sQuery(id+"F0.wireOp",EDGE,"E9.15.2"),sQuery(id+"F0.wireOp",EDGE,"E9.15.3"),sQuery(id+"F0.wireOp",EDGE,"E9.15.4"),sQuery(id+"F0.wireOp",EDGE,"E9.15.7"),sQuery(id+"F0.wireOp",EDGE,"E9.15.9"),sQuery(id+"F0.wireOp",EDGE,"E9.15.10"),sQuery(id+"F0.wireOp",EDGE,"E9.15.12"),sQuery(id+"F0.wireOp",EDGE,"E10")])]});
            deleteBodies(context, id + "F3", {"entities" : qUnion([Q0])});
        }
        {
            var Q0;
            Q0 = qSketchRegion(id + "F2", true);
            extrude(context, id + "F4", {"entities" : qUnion([Q0]), "depth" : 1.5 * mm, "offsetDistance" : 25 * mm});
        }
        {
            var Q0;
            Q0=makeQuery(id+"F4.opExtrude","CAP_FACE",FACE,{"disambiguationData":[OSD([sQuery(id+"F2.wireOp",EDGE,"E11"),sQuery(id+"F2.wireOp",EDGE,"E14"),sQuery(id+"F2.wireOp",EDGE,"E15"),sQuery(id+"F2.wireOp",EDGE,"E16"),sQuery(id+"F2.wireOp",EDGE,"E17"),sQuery(id+"F2.wireOp",EDGE,"E18"),sQuery(id+"F2.wireOp",EDGE,"E19"),sQuery(id+"F2.wireOp",EDGE,"E20.trimOffspring"),sQuery(id+"F2.wireOp",EDGE,"E21.trimOffspring"),sQuery(id+"F2.wireOp",EDGE,"E22")])],"isStart":true});
            var sketch = newSketch(context, id + "F5", { "sketchPlane" : qUnion([Q0])});
            skLineSegment(sketch, "E24", {"start": v(-64.62, -25.34) * mm, "end": v(-62.95, -35.68) * mm});
            skLineSegment(sketch, "E25", {"start": v(-62.95, -35.68) * mm, "end": v(-77.88, -38.72) * mm});
            skLineSegment(sketch, "E26", {"start": v(-77.88, -38.72) * mm, "end": v(-81.07, -26.63) * mm});
            skLineSegment(sketch, "E27", {"start": v(-81.07, -26.63) * mm, "end": v(-64.62, -25.34) * mm});
            skSolve(sketch);
        }
        {
            var Q0;
            Q0 = qSketchRegion(id + "F5", true);
            extrude(context, id + "F6", {"entities" : qUnion([Q0]), "operationType" : NewBodyOperationType.ADD, "depth" : 2 * mm, "offsetDistance" : 25 * mm});
        }
        {
            var Q0;
            Q0=makeQuery(id+"F4.opExtrude","CAP_FACE",FACE,{"disambiguationData":[OSD([sQuery(id+"F2.wireOp",EDGE,"E11"),sQuery(id+"F2.wireOp",EDGE,"E14"),sQuery(id+"F2.wireOp",EDGE,"E15"),sQuery(id+"F2.wireOp",EDGE,"E16"),sQuery(id+"F2.wireOp",EDGE,"E17"),sQuery(id+"F2.wireOp",EDGE,"E18"),sQuery(id+"F2.wireOp",EDGE,"E19"),sQuery(id+"F2.wireOp",EDGE,"E20.trimOffspring"),sQuery(id+"F2.wireOp",EDGE,"E21.trimOffspring"),sQuery(id+"F2.wireOp",EDGE,"E22")])],"isStart":false});
            var sketch = newSketch(context, id + "F7", { "sketchPlane" : qUnion([Q0])});
            skLineSegment(sketch, "E28", {"start": v(81.07, -26.63) * mm, "end": v(64.62, -25.34) * mm});
            skLineSegment(sketch, "E29", {"start": v(64.62, -25.34) * mm, "end": v(62.95, -35.68) * mm});
            skLineSegment(sketch, "E30", {"start": v(62.95, -35.68) * mm, "end": v(77.88, -38.72) * mm});
            skLineSegment(sketch, "E31", {"start": v(77.88, -38.72) * mm, "end": v(81.07, -26.63) * mm});
            skSolve(sketch);
        }
        {
            var Q0;
            Q0 = qSketchRegion(id + "F7", true);
            extrude(context, id + "F8", {"entities" : qUnion([Q0]), "operationType" : NewBodyOperationType.ADD, "depth" : 9.8 * mm, "offsetDistance" : 25 * mm});
        }
        {
            var Q0;
            Q0=qCreatedBy(makeId("Front.planeOp"),FACE);
            var sketch = newSketch(context, id + "F9", { "sketchPlane" : qUnion([Q0])});
            skLineSegment(sketch, "E32", {"start": v(0, 0) * mm, "end": v(0, -28.79) * mm});
            skLineSegment(sketch, "E33", {"start": v(0, -28.79) * mm, "end": v(70.88, -28.79) * mm});
            skCircle(sketch, "E34", {"center": v(70.88, -28.79) * mm, "radius": 1.4 * mm});
            skSolve(sketch);
        }
        {
            var Q0;
            Q0 = qSketchRegion(id + "F9", true);
            extrude(context, id + "F10", {"entities" : qUnion([Q0]), "operationType" : NewBodyOperationType.REMOVE, "depth" : 25 * mm, "offsetDistance" : 25 * mm});
        }
    });
